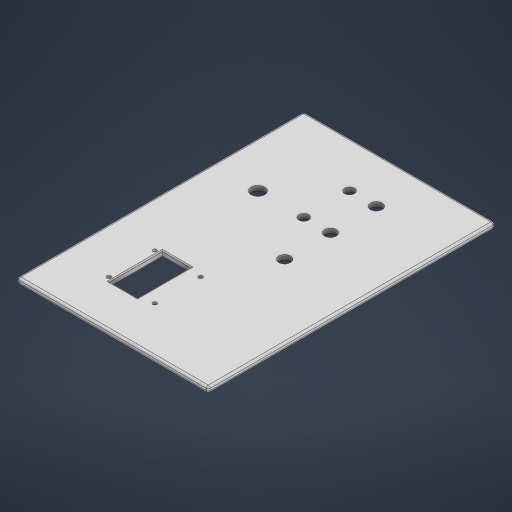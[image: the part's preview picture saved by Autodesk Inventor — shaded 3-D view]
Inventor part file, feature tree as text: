
AUTODESK INVENTOR PART (.ipt)
format: ipt  version: 2024.2 (Build 282272000, 272)  size: 311,296 bytes
history: native  units: mm
features: extrude x3, sketch x3, fillet x2, projected_geometry x1
ambient origin geometry x8: Origin, YZ Plane, XZ Plane, XY Plane, X Axis, Y Axis, Z Axis, Center Point
bodies: Solid1 (feature_tree)
feature tree (9):
  extrude  "Extrusion1"  Depth=150.0mm
  extrude  "Extrusion2"  Depth=3.25mm
  fillet  "Fillet1"  Radius=3.25mm
  extrude  "Extrusion4"  Depth=3.25mm
  fillet  "Fillet2"  Radius=3.0mm
  sketch  "Sketch1"  dims[d0=100.0mm d1=150.0mm]
  sketch  "Sketch2"  dims[d2=3.0mm d3=0.0mm d4=3.25mm d5=3.25mm]
  projected_geometry  "Projected Loop1"
  sketch  "Sketch4"  dims[d6=3.25mm d7=3.25mm d8=3.0mm d9=0.0mm d10=2.0mm d11=1.0mm d12=3.0mm d13=3.0mm d14=3.0mm d15=3.0mm d16=2.0mm d19=5.0mm d20=5.0mm d21=6.0mm d22=6.0mm d23=6.0mm d24=7.0mm d25=2.0mm d26=2.0mm d27=2.0mm d28=2.0mm d29=24.0mm d30=24.0mm d31=24.0mm d32=24.0mm d33=33.941mm d34=0.0mm d35=24.0mm d36=24.0mm d37=14.0mm d38=14.0mm d39=24.0mm d40=14.0mm d41=24.0mm d42=24.0mm d43=38.0mm d46=48.0mm d47=24.0mm d48=24.0mm d49=15.0mm d50=28.0mm d51=2.0mm d52=2.0mm d53=2.0mm d54=10.0mm d55=0.0mm d56=0.5mm]
